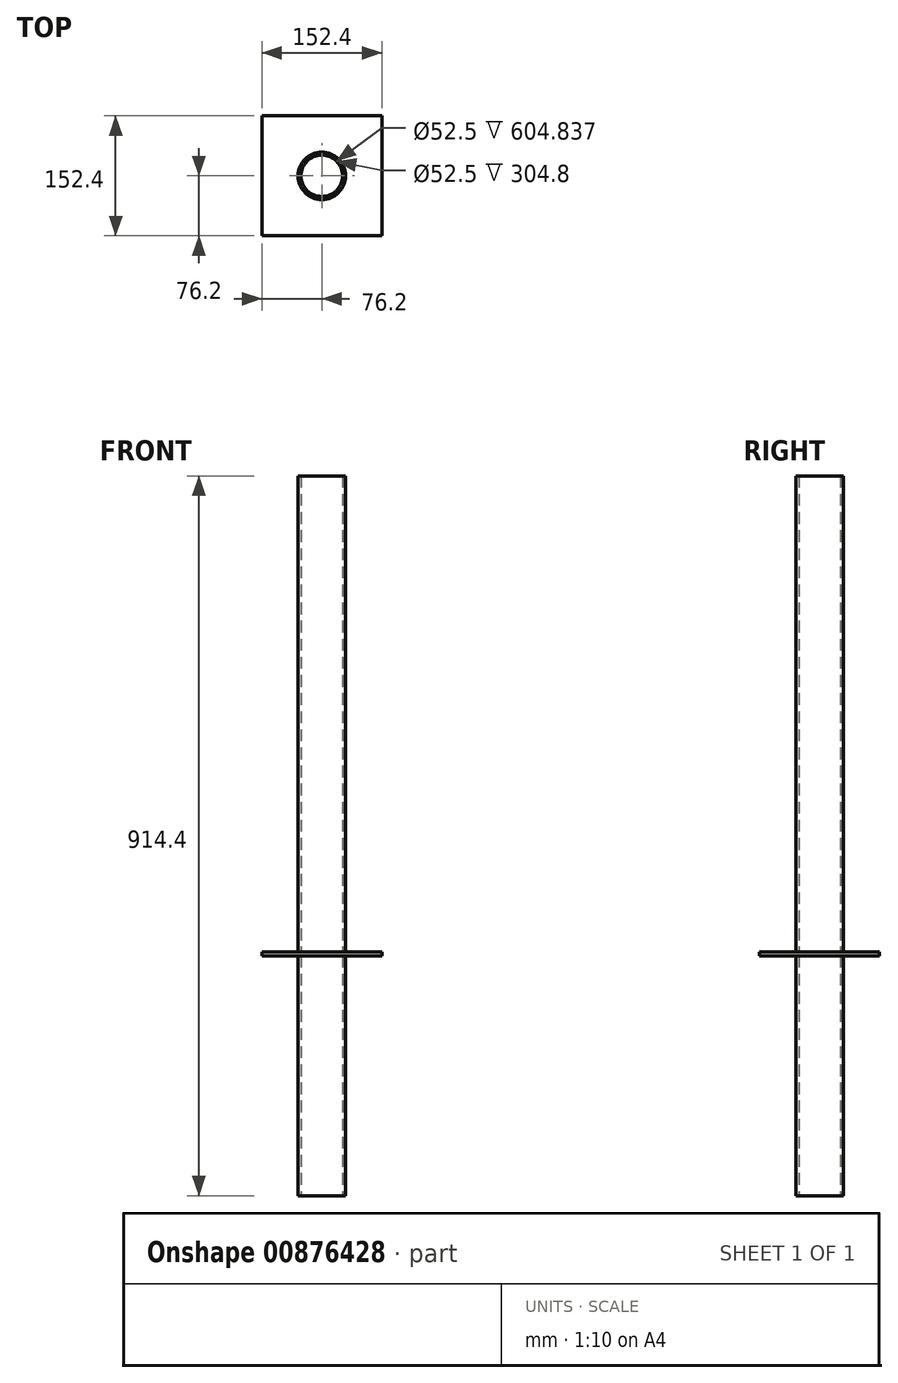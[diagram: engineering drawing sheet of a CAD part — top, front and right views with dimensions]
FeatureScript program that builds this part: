
annotation { "Feature Type Name" : "Feature", "Feature Type Description" : "" }
export const myFeature = defineFeature(function(context is Context, id is Id, definition is map)
    precondition{}
    {
        {
            var Q0;
            Q0=qCreatedBy(makeId("Top.planeOp"),FACE);
            var sketch = newSketch(context, id + "F0", { "sketchPlane" : qUnion([Q0])});
            skCircle(sketch, "E0", {"center": v(0, 0) * mm, "radius": 30.16 * mm});
            skCircle(sketch, "E1", {"center": v(0, 0) * mm, "radius": 26.25 * mm});
            skSolve(sketch);
        }
        {
            var Q0;
            Q0 = qSketchRegion(id + "F0", true);
            extrude(context, id + "F1", {"entities" : qUnion([Q0]), "depth" : 914.4 * mm, "offsetDistance" : 25.4 * mm});
        }
        {
            var Q0;
            Q0=qCreatedBy(makeId("Top.planeOp"),FACE);
            cPlane(context, id + "F2", {"entities" : qUnion([Q0]), "cplaneType" : CPlaneType.OFFSET, "offset" : 304.8 * mm, "width" : 152.4 * mm, "height" : 152.4 * mm});
        }
        {
            var Q0;
            Q0=qCreatedBy(id+"F2.planeOp",FACE);
            var sketch = newSketch(context, id + "F3", { "sketchPlane" : qUnion([Q0])});
            skLineSegment(sketch, "E2.bottom", {"start": v(-76.2, 76.2) * mm, "end": v(76.2, 76.2) * mm});
            skLineSegment(sketch, "E2.top", {"start": v(-76.2, -76.2) * mm, "end": v(76.2, -76.2) * mm});
            skLineSegment(sketch, "E2.left", {"start": v(-76.2, 76.2) * mm, "end": v(-76.2, -76.2) * mm});
            skLineSegment(sketch, "E2.right", {"start": v(76.2, 76.2) * mm, "end": v(76.2, -76.2) * mm});
            skLineSegment(sketch, "E3", {"start": v(-76.2, 76.2) * mm, "end": v(76.2, -76.2) * mm, "construction": true});
            skLineSegment(sketch, "E4", {"start": v(76.2, 76.2) * mm, "end": v(-76.2, -76.2) * mm, "construction": true});
            skPoint(sketch, "E5", {"position": v(0, 0) * mm});
            skSolve(sketch);
        }
        {
            var Q0;
            Q0=makeQuery(id+"F3.imprint","IMPRINT",FACE,{"disambiguationData":[TD([[makeQuery(id+"F3.imprint","IMPRINT",EDGE,{"derivedFrom":sQuery(id+"F3.wireOp",EDGE,"E2.bottom")}),-1.0]])]});
            extrude(context, id + "F4", {"entities" : qUnion([Q0]), "operationType" : NewBodyOperationType.ADD, "depth" : 4.76 * mm, "offsetDistance" : 25.4 * mm});
        }
    });
